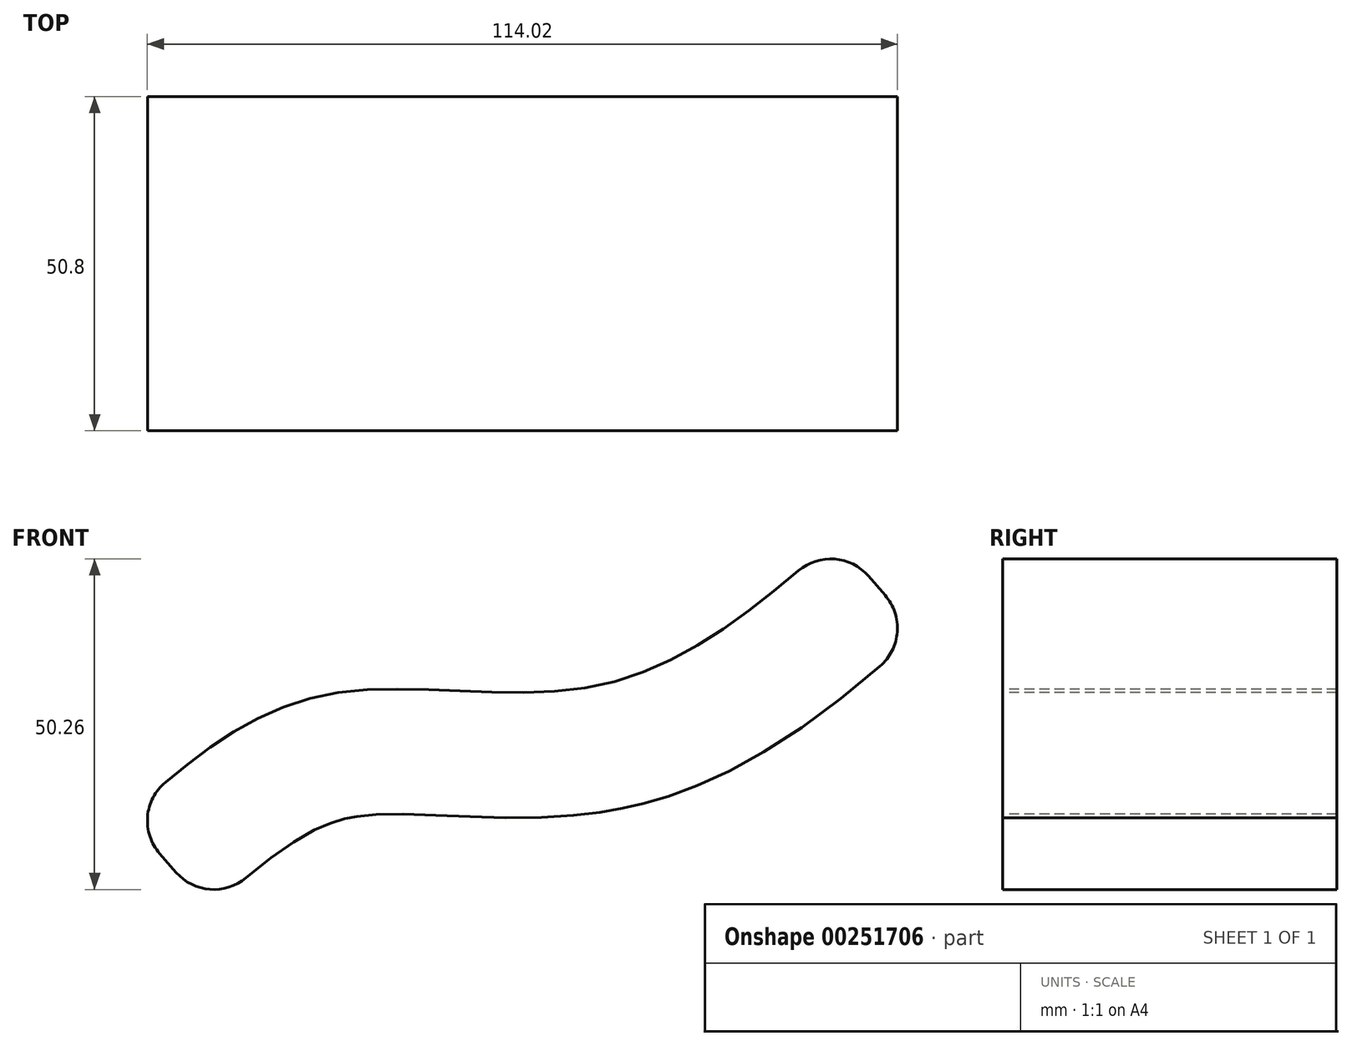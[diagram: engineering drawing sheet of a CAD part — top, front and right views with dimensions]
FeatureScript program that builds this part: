
annotation { "Feature Type Name" : "Feature", "Feature Type Description" : "" }
export const myFeature = defineFeature(function(context is Context, id is Id, definition is map)
    precondition{}
    {
        {
            var Q0;
            Q0=qCreatedBy(makeId("Front.planeOp"),FACE);
            var sketch = newSketch(context, id + "F0", { "sketchPlane" : qUnion([Q0])});
            skFitSpline(sketch, "E0", {"points": [v(-46.17, 0) * mm, v(-16.42, 18.28) * mm, v(25.72, 19.83) * mm, v(61.66, 42.14) * mm], "startDerivative": vector(87, 76.1) * mm, "endDerivative": vector(97.68, 84.79) * mm});
            skFitSpline(sketch, "E1.0", {"points": [v(-33.63, -14.34) * mm, v(-31.81, -12.75) * mm, v(-29.23, -10.5) * mm, v(-26.02, -7.86) * mm, v(-23.74, -6.09) * mm, v(-21.57, -4.54) * mm, v(-19.53, -3.25) * mm, v(-17.94, -2.37) * mm, v(-16.73, -1.78) * mm, v(-15.85, -1.4) * mm, v(-15, -1.07) * mm, v(-14.16, -0.79) * mm, v(-13.48, -0.6) * mm, v(-12.93, -0.46) * mm, v(-12.53, -0.37) * mm, v(-12.11, -0.28) * mm, v(-11.5, -0.18) * mm, v(-10.65, -0.06) * mm, v(-9.5, 0.05) * mm, v(-7.81, 0.17) * mm, v(-5.4, 0.22) * mm, v(-2.1, 0.17) * mm, v(1.58, 0.04) * mm, v(5.57, -0.14) * mm, v(9.85, -0.29) * mm, v(14.4, -0.34) * mm, v(18.43, -0.22) * mm, v(21.78, 0.02) * mm, v(24.36, 0.3) * mm, v(26.56, 0.6) * mm, v(28.35, 0.92) * mm, v(29.7, 1.2) * mm, v(31.06, 1.5) * mm, v(32.84, 1.95) * mm, v(35.02, 2.57) * mm, v(37.57, 3.42) * mm, v(40.86, 4.67) * mm, v(44.78, 6.43) * mm, v(49.2, 8.8) * mm, v(54.73, 12.18) * mm, v(61.04, 16.72) * mm, v(67.9, 22.33) * mm, v(72.11, 25.99) * mm, v(74.15, 27.75) * mm]});
            skLineSegment(sketch, "E2", {"start": v(-46.17, 0) * mm, "end": v(-33.63, -14.34) * mm});
            skLineSegment(sketch, "E3", {"start": v(61.66, 42.14) * mm, "end": v(74.15, 27.75) * mm});
            skSolve(sketch);
        }
        {
            var Q0;
            Q0 = qSketchRegion(id + "F0", true);
            extrude(context, id + "F1", {"entities" : qUnion([Q0]), "depth" : 50.8 * mm});
        }
        {
            var Q0;
            Q0=makeQuery(id+"F1.opExtrude","SWEPT_EDGE",EDGE,{"disambiguationData":[OSD([sQuery(id+"F0.wireOp",EDGE,"E0"),sQuery(id+"F0.wireOp",EDGE,"E3")])]});
            var Q1;
            Q1=makeQuery(id+"F1.opExtrude","SWEPT_EDGE",EDGE,{"disambiguationData":[OSD([sQuery(id+"F0.wireOp",EDGE,"E1.0"),sQuery(id+"F0.wireOp",EDGE,"E3")])]});
            var Q2;
            Q2=makeQuery(id+"F1.opExtrude","SWEPT_EDGE",EDGE,{"disambiguationData":[OSD([sQuery(id+"F0.wireOp",EDGE,"E0"),sQuery(id+"F0.wireOp",EDGE,"E2")])]});
            var Q3;
            Q3=makeQuery(id+"F1.opExtrude","SWEPT_EDGE",EDGE,{"disambiguationData":[OSD([sQuery(id+"F0.wireOp",EDGE,"E1.0"),sQuery(id+"F0.wireOp",EDGE,"E2")])]});
            fillet(context, id + "F2", {"entities" : qUnion([Q0, Q1, Q2, Q3]), "radius" : 7.62 * mm, "tangentPropagation" : true, "allowEdgeOverflow" : false});
        }
    });
